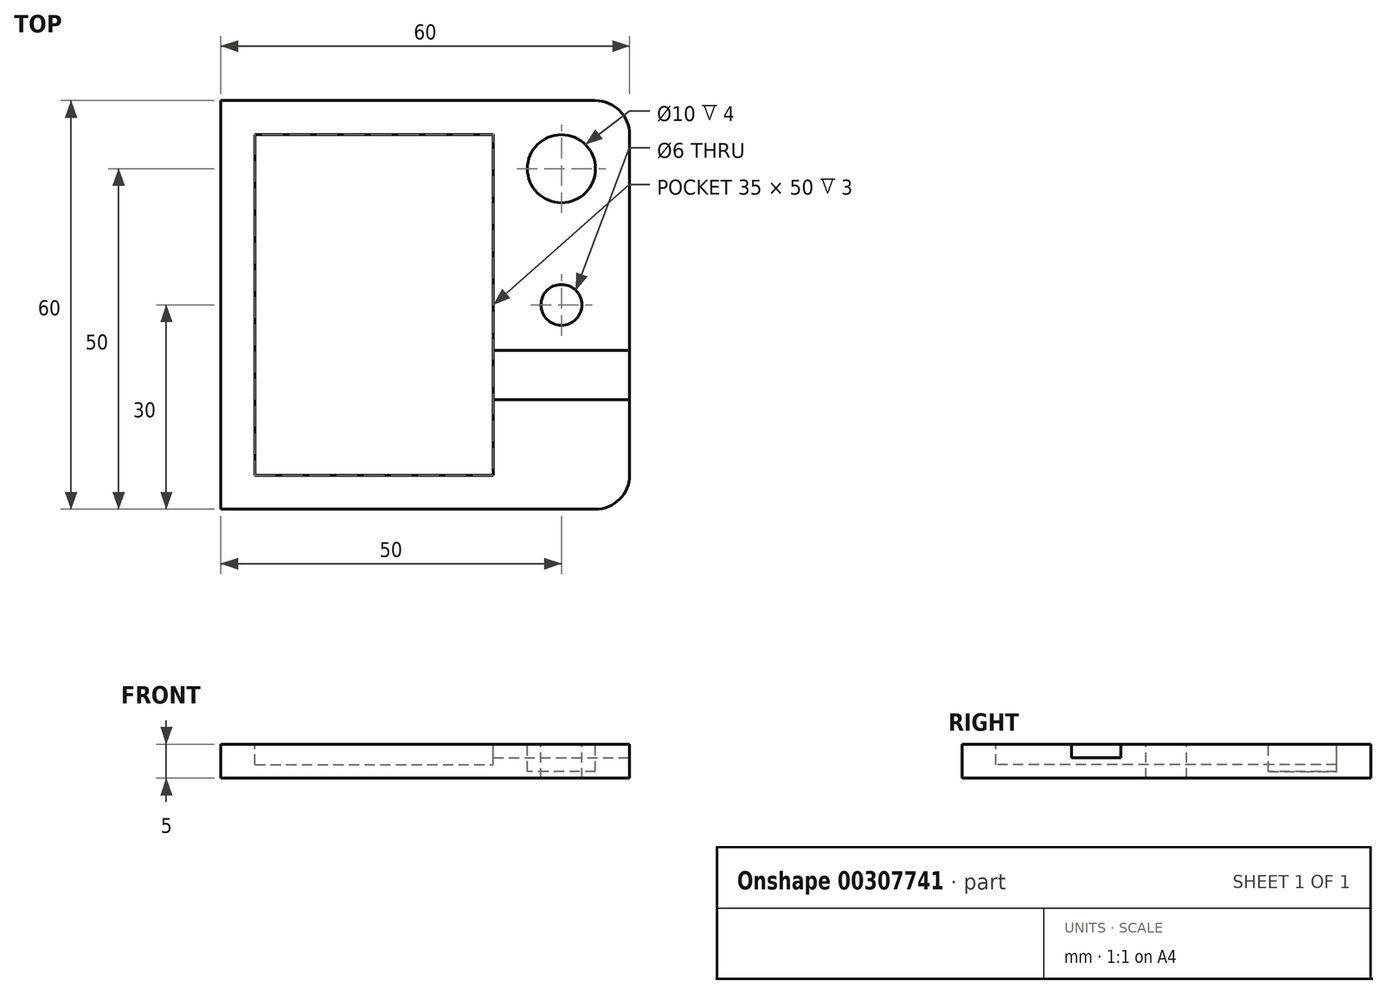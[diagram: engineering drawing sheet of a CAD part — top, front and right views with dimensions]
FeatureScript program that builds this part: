
annotation { "Feature Type Name" : "Feature", "Feature Type Description" : "" }
export const myFeature = defineFeature(function(context is Context, id is Id, definition is map)
    precondition{}
    {
        {
            var Q0;
            Q0=qCreatedBy(makeId("Top.planeOp"),FACE);
            var sketch = newSketch(context, id + "F0", { "sketchPlane" : qUnion([Q0])});
            skLineSegment(sketch, "E0.bottom", {"start": v(0, 0) * mm, "end": v(60, 0) * mm});
            skLineSegment(sketch, "E0.top", {"start": v(0, -60) * mm, "end": v(60, -60) * mm});
            skLineSegment(sketch, "E0.left", {"start": v(0, 0) * mm, "end": v(0, -60) * mm});
            skLineSegment(sketch, "E0.right", {"start": v(60, 0) * mm, "end": v(60, -60) * mm});
            skSolve(sketch);
        }
        {
            var Q0;
            Q0=makeQuery(id+"F0.imprint","IMPRINT",FACE,{"disambiguationData":[TD([[makeQuery(id+"F0.imprint","IMPRINT",EDGE,{"derivedFrom":sQuery(id+"F0.wireOp",EDGE,"E0.bottom")}),-1.0]])]});
            extrude(context, id + "F1", {"entities" : qUnion([Q0]), "depth" : 5 * mm});
        }
        {
            var Q0;
            Q0=makeQuery(id+"F1.opExtrude","SWEPT_EDGE",EDGE,{"disambiguationData":[OSD([sQuery(id+"F0.wireOp",EDGE,"E0.bottom"),sQuery(id+"F0.wireOp",EDGE,"E0.right")])]});
            var Q1;
            Q1=makeQuery(id+"F1.opExtrude","SWEPT_EDGE",EDGE,{"disambiguationData":[OSD([sQuery(id+"F0.wireOp",EDGE,"E0.top"),sQuery(id+"F0.wireOp",EDGE,"E0.right")])]});
            fillet(context, id + "F2", {"entities" : qUnion([Q0, Q1]), "radius" : 5 * mm, "tangentPropagation" : true, "allowEdgeOverflow" : false});
        }
        {
            var Q0;
            Q0=makeQuery(id+"F1.opExtrude","CAP_FACE",FACE,{"disambiguationData":[OSD([sQuery(id+"F0.wireOp",EDGE,"E0.bottom"),sQuery(id+"F0.wireOp",EDGE,"E0.top"),sQuery(id+"F0.wireOp",EDGE,"E0.left"),sQuery(id+"F0.wireOp",EDGE,"E0.right")])],"isStart":false});
            var sketch = newSketch(context, id + "F3", { "sketchPlane" : qUnion([Q0])});
            skCircle(sketch, "E1", {"center": v(50, -10) * mm, "radius": 5 * mm});
            skLineSegment(sketch, "E2", {"start": v(50, -10) * mm, "end": v(50, 0) * mm, "construction": true});
            skLineSegment(sketch, "E3", {"start": v(50, -10) * mm, "end": v(60, -10) * mm, "construction": true});
            skLineSegment(sketch, "E4.bottom", {"start": v(5, -5) * mm, "end": v(40, -5) * mm});
            skLineSegment(sketch, "E4.top", {"start": v(5, -55) * mm, "end": v(40, -55) * mm});
            skLineSegment(sketch, "E4.left", {"start": v(5, -5) * mm, "end": v(5, -55) * mm});
            skLineSegment(sketch, "E4.right", {"start": v(40, -5) * mm, "end": v(40, -36.66) * mm});
            skCircle(sketch, "E5", {"center": v(50, -30) * mm, "radius": 3 * mm});
            skPoint(sketch, "E5.centerSnap0", {"position": v(60, -30) * mm});
            skLineSegment(sketch, "E6", {"start": v(50, -10) * mm, "end": v(50, -30) * mm, "construction": true});
            skLineSegment(sketch, "E7", {"start": v(40, -36.66) * mm, "end": v(60, -36.66) * mm});
            skLineSegment(sketch, "E8", {"start": v(40, -43.89) * mm, "end": v(40, -43.89) * mm});
            skLineSegment(sketch, "E9", {"start": v(40, -36.66) * mm, "end": v(40, -43.89) * mm});
            skLineSegment(sketch, "E10", {"start": v(40, -43.89) * mm, "end": v(60, -43.89) * mm});
            skLineSegment(sketch, "E11", {"start": v(40, -43.89) * mm, "end": v(40, -55) * mm});
            skSolve(sketch);
        }
        {
            var Q0;
            Q0=makeQuery(id+"F3.imprint","IMPRINT",FACE,{"disambiguationData":[TD([[makeQuery(id+"F3.imprint","IMPRINT",EDGE,{"derivedFrom":sQuery(id+"F3.wireOp",EDGE,"E4.bottom")}),-1.0]])]});
            extrude(context, id + "F4", {"entities" : qUnion([Q0]), "operationType" : NewBodyOperationType.REMOVE, "oppositeDirection" : true, "depth" : 3 * mm});
        }
        {
            var Q0;
            Q0=makeQuery(id+"F3.imprint","IMPRINT",FACE,{"disambiguationData":[TD([[makeQuery(id+"F3.imprint","IMPRINT",EDGE,{"derivedFrom":sQuery(id+"F3.wireOp",EDGE,"E1")}),1.0]])]});
            extrude(context, id + "F5", {"entities" : qUnion([Q0]), "operationType" : NewBodyOperationType.REMOVE, "oppositeDirection" : true, "depth" : 4 * mm});
        }
        {
            var Q0;
            Q0=makeQuery(id+"F3.imprint","IMPRINT",FACE,{"disambiguationData":[TD([[makeQuery(id+"F3.imprint","IMPRINT",EDGE,{"derivedFrom":sQuery(id+"F3.wireOp",EDGE,"E5")}),1.0]])]});
            extrude(context, id + "F6", {"entities" : qUnion([Q0]), "operationType" : NewBodyOperationType.REMOVE, "oppositeDirection" : true, "depth" : 5 * mm});
        }
        {
            var Q0;
            {var subQ0=sQuery(id+"F3.wireOp",EDGE,"E7");Q0=makeQuery(id+"F3.imprint","IMPRINT",FACE,{"disambiguationData":[TD([[makeQuery(id+"F3.imprint","IMPRINT",EDGE,{"derivedFrom":subQ0}),-1.0]])]});}
            extrude(context, id + "F7", {"entities" : qUnion([Q0]), "operationType" : NewBodyOperationType.REMOVE, "oppositeDirection" : true, "depth" : 2 * mm});
        }
    });
